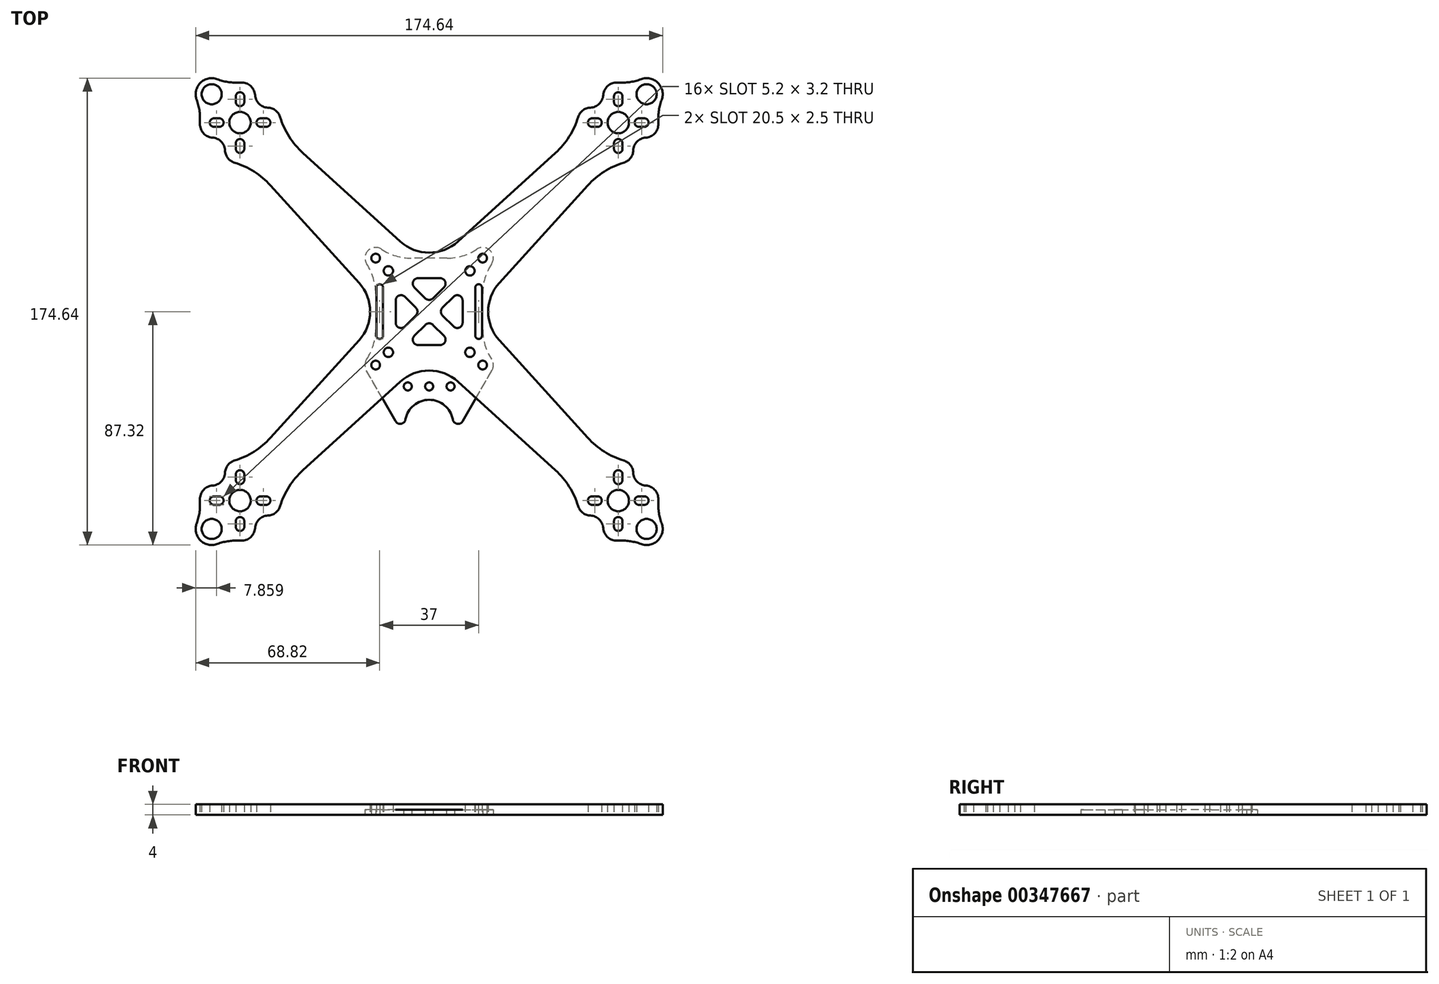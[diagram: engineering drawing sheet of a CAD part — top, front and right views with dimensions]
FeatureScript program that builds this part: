
annotation { "Feature Type Name" : "Feature", "Feature Type Description" : "" }
export const myFeature = defineFeature(function(context is Context, id is Id, definition is map)
    precondition{}
    {
        {
            var Q0;
            Q0=qCreatedBy(makeId("Top.planeOp"),FACE);
            var sketch = newSketch(context, id + "F0", { "sketchPlane" : qUnion([Q0])});
            skCircle(sketch, "E0", {"center": v(0, 0) * mm, "radius": 100 * mm, "construction": true});
            skArc(sketch, "E1", {"start": v(-59.34, 80.5) * mm, "mid": v(-59.71, 80.91) * mm, "end": v(-60.1, 81.32) * mm, "construction": true});
            skCircle(sketch, "E2", {"center": v(-70.71, 70.71) * mm, "radius": 4 * mm});
            skLineSegment(sketch, "E3", {"start": v(-70.71, 70.71) * mm, "end": v(0, 0) * mm, "construction": true});
            skCircle(sketch, "E4", {"center": v(-15.25, 15.25) * mm, "radius": 1.75 * mm});
            skCircle(sketch, "E5", {"center": v(-70.71, 70.71) * mm, "radius": 64.25 * mm, "construction": true});
            skCircle(sketch, "E6", {"center": v(-20, 20) * mm, "radius": 1.63 * mm});
            skCircle(sketch, "E7.MirrorC", {"center": v(20, 20) * mm, "radius": 1.63 * mm});
            skCircle(sketch, "E8.MirrorC", {"center": v(15.25, 15.25) * mm, "radius": 1.75 * mm});
            skCircle(sketch, "E9.MirrorC", {"center": v(-20, -20) * mm, "radius": 1.63 * mm});
            skCircle(sketch, "E10.MirrorC", {"center": v(20, -20) * mm, "radius": 1.63 * mm});
            skCircle(sketch, "E11.MirrorC", {"center": v(15.25, -15.25) * mm, "radius": 1.75 * mm});
            skCircle(sketch, "E12.MirrorC", {"center": v(-15.25, -15.25) * mm, "radius": 1.75 * mm});
            skArc(sketch, "E13.MirrorCS", {"start": v(59.34, 80.5) * mm, "mid": v(59.71, 80.91) * mm, "end": v(60.1, 81.32) * mm, "construction": true});
            skCircle(sketch, "E14.MirrorC", {"center": v(70.71, 70.71) * mm, "radius": 4 * mm});
            skArc(sketch, "E15.MirrorCS", {"start": v(-59.34, -80.5) * mm, "mid": v(-59.71, -80.91) * mm, "end": v(-60.1, -81.32) * mm, "construction": true});
            skCircle(sketch, "E16.MirrorC", {"center": v(-70.71, -70.71) * mm, "radius": 4 * mm});
            skArc(sketch, "E17.MirrorCS", {"start": v(59.34, -80.5) * mm, "mid": v(59.71, -80.91) * mm, "end": v(60.1, -81.32) * mm, "construction": true});
            skCircle(sketch, "E18.MirrorC", {"center": v(70.71, -70.71) * mm, "radius": 4 * mm});
            skLineSegment(sketch, "E19", {"start": v(-18.5, 9) * mm, "end": v(-18.5, -9) * mm, "construction": true});
            skArc(sketch, "E20.0.startCap", {"start": v(-19.75, 9) * mm, "mid": v(-18.5, 10.25) * mm, "end": v(-17.25, 9) * mm});
            skArc(sketch, "E20.0.endCap", {"start": v(-17.25, -9) * mm, "mid": v(-18.5, -10.25) * mm, "end": v(-19.75, -9) * mm});
            skLineSegment(sketch, "E20.0.left", {"start": v(-17.25, 9) * mm, "end": v(-17.25, -9) * mm});
            skLineSegment(sketch, "E20.0.right", {"start": v(-19.75, 9) * mm, "end": v(-19.75, -9) * mm});
            skLineSegment(sketch, "E21.MirrorCS", {"start": v(17.25, 9) * mm, "end": v(17.25, -9) * mm});
            skLineSegment(sketch, "E22.MirrorCS", {"start": v(18.5, 9) * mm, "end": v(18.5, -9) * mm, "construction": true});
            skArc(sketch, "E23.MirrorCS", {"start": v(17.25, -9) * mm, "mid": v(18.5, -10.25) * mm, "end": v(19.75, -9) * mm});
            skArc(sketch, "E24.MirrorCS", {"start": v(19.75, 9) * mm, "mid": v(18.5, 10.25) * mm, "end": v(17.25, 9) * mm});
            skLineSegment(sketch, "E25.MirrorCS", {"start": v(19.75, 9) * mm, "end": v(19.75, -9) * mm});
            skLineSegment(sketch, "E26", {"start": v(-12.5, 4.14) * mm, "end": v(-12.5, -4.14) * mm});
            skLineSegment(sketch, "E27", {"start": v(-9.09, -5.55) * mm, "end": v(-4.95, -1.41) * mm});
            skLineSegment(sketch, "E28", {"start": v(-4.95, 1.41) * mm, "end": v(-9.09, 5.55) * mm});
            skPoint(sketch, "E29.visualSharp", {"position": v(-12.5, 8.96) * mm});
            skArc(sketch, "E29.filletArc", {"start": v(-9.09, 5.55) * mm, "mid": v(-11.27, 5.98) * mm, "end": v(-12.5, 4.14) * mm});
            skPoint(sketch, "E30.visualSharp", {"position": v(-12.5, -8.96) * mm});
            skArc(sketch, "E30.filletArc", {"start": v(-12.5, -4.14) * mm, "mid": v(-11.27, -5.98) * mm, "end": v(-9.09, -5.55) * mm});
            skPoint(sketch, "E31.visualSharp", {"position": v(-3.54, 0) * mm});
            skArc(sketch, "E31.filletArc", {"start": v(-4.95, -1.41) * mm, "mid": v(-4.36, 0) * mm, "end": v(-4.95, 1.41) * mm});
            skArc(sketch, "E32.1.0", {"start": v(4.14, -12.5) * mm, "mid": v(5.98, -11.27) * mm, "end": v(5.55, -9.09) * mm});
            skPoint(sketch, "E32.1.1", {"position": v(0, -3.54) * mm});
            skLineSegment(sketch, "E32.1.2", {"start": v(-1.41, -4.95) * mm, "end": v(-5.55, -9.09) * mm});
            skArc(sketch, "E32.1.3", {"start": v(-5.55, -9.09) * mm, "mid": v(-5.98, -11.27) * mm, "end": v(-4.14, -12.5) * mm});
            skLineSegment(sketch, "E32.1.4", {"start": v(5.55, -9.09) * mm, "end": v(1.41, -4.95) * mm});
            skLineSegment(sketch, "E32.1.5", {"start": v(-4.14, -12.5) * mm, "end": v(4.14, -12.5) * mm});
            skArc(sketch, "E32.1.6", {"start": v(1.41, -4.95) * mm, "mid": v(0, -4.36) * mm, "end": v(-1.41, -4.95) * mm});
            skArc(sketch, "E32.2.0", {"start": v(12.5, 4.14) * mm, "mid": v(11.27, 5.98) * mm, "end": v(9.09, 5.55) * mm});
            skPoint(sketch, "E32.2.1", {"position": v(3.54, 0) * mm});
            skLineSegment(sketch, "E32.2.2", {"start": v(4.95, -1.41) * mm, "end": v(9.09, -5.55) * mm});
            skArc(sketch, "E32.2.3", {"start": v(9.09, -5.55) * mm, "mid": v(11.27, -5.98) * mm, "end": v(12.5, -4.14) * mm});
            skLineSegment(sketch, "E32.2.4", {"start": v(9.09, 5.55) * mm, "end": v(4.95, 1.41) * mm});
            skLineSegment(sketch, "E32.2.5", {"start": v(12.5, -4.14) * mm, "end": v(12.5, 4.14) * mm});
            skArc(sketch, "E32.2.6", {"start": v(4.95, 1.41) * mm, "mid": v(4.36, 0) * mm, "end": v(4.95, -1.41) * mm});
            skArc(sketch, "E32.3.0", {"start": v(-4.14, 12.5) * mm, "mid": v(-5.98, 11.27) * mm, "end": v(-5.55, 9.09) * mm});
            skPoint(sketch, "E32.3.1", {"position": v(0, 3.54) * mm});
            skLineSegment(sketch, "E32.3.2", {"start": v(1.41, 4.95) * mm, "end": v(5.55, 9.09) * mm});
            skArc(sketch, "E32.3.3", {"start": v(5.55, 9.09) * mm, "mid": v(5.98, 11.27) * mm, "end": v(4.14, 12.5) * mm});
            skLineSegment(sketch, "E32.3.4", {"start": v(-5.55, 9.09) * mm, "end": v(-1.41, 4.95) * mm});
            skLineSegment(sketch, "E32.3.5", {"start": v(4.14, 12.5) * mm, "end": v(-4.14, 12.5) * mm});
            skArc(sketch, "E32.3.6", {"start": v(-1.41, 4.95) * mm, "mid": v(0, 4.36) * mm, "end": v(1.41, 4.95) * mm});
            skCircle(sketch, "E33", {"center": v(-70.71, 70.71) * mm, "radius": 7.75 * mm, "construction": true});
            skCircle(sketch, "E34", {"center": v(-70.71, 70.71) * mm, "radius": 9.75 * mm, "construction": true});
            skLineSegment(sketch, "E35", {"start": v(-70.71, 70.71) * mm, "end": v(-70.71, 78.46) * mm, "construction": true});
            skLineSegment(sketch, "E36", {"start": v(-70.71, 78.46) * mm, "end": v(-70.71, 80.46) * mm, "construction": true});
            skArc(sketch, "E37.0.startCap", {"start": v(-69.11, 78.46) * mm, "mid": v(-70.71, 76.86) * mm, "end": v(-72.31, 78.46) * mm});
            skArc(sketch, "E37.0.endCap", {"start": v(-72.31, 80.46) * mm, "mid": v(-70.71, 82.06) * mm, "end": v(-69.11, 80.46) * mm});
            skLineSegment(sketch, "E37.0.left", {"start": v(-72.31, 78.46) * mm, "end": v(-72.31, 80.46) * mm});
            skLineSegment(sketch, "E37.0.right", {"start": v(-69.11, 78.46) * mm, "end": v(-69.11, 80.46) * mm});
            skLineSegment(sketch, "E38.1.0", {"start": v(-78.46, 72.31) * mm, "end": v(-80.46, 72.31) * mm});
            skLineSegment(sketch, "E38.1.1", {"start": v(-78.46, 69.11) * mm, "end": v(-80.46, 69.11) * mm});
            skArc(sketch, "E38.1.2", {"start": v(-80.46, 69.11) * mm, "mid": v(-82.06, 70.71) * mm, "end": v(-80.46, 72.31) * mm});
            skArc(sketch, "E38.1.3", {"start": v(-78.46, 72.31) * mm, "mid": v(-76.86, 70.71) * mm, "end": v(-78.46, 69.11) * mm});
            skLineSegment(sketch, "E38.1.4", {"start": v(-78.46, 70.71) * mm, "end": v(-80.46, 70.71) * mm, "construction": true});
            skLineSegment(sketch, "E38.2.0", {"start": v(-72.31, 62.96) * mm, "end": v(-72.31, 60.96) * mm});
            skLineSegment(sketch, "E38.2.1", {"start": v(-69.11, 62.96) * mm, "end": v(-69.11, 60.96) * mm});
            skArc(sketch, "E38.2.2", {"start": v(-69.11, 60.96) * mm, "mid": v(-70.71, 59.36) * mm, "end": v(-72.31, 60.96) * mm});
            skArc(sketch, "E38.2.3", {"start": v(-72.31, 62.96) * mm, "mid": v(-70.71, 64.56) * mm, "end": v(-69.11, 62.96) * mm});
            skLineSegment(sketch, "E38.2.4", {"start": v(-70.71, 62.96) * mm, "end": v(-70.71, 60.96) * mm, "construction": true});
            skLineSegment(sketch, "E38.3.0", {"start": v(-62.96, 69.11) * mm, "end": v(-60.96, 69.11) * mm});
            skLineSegment(sketch, "E38.3.1", {"start": v(-62.96, 72.31) * mm, "end": v(-60.96, 72.31) * mm});
            skArc(sketch, "E38.3.2", {"start": v(-60.96, 72.31) * mm, "mid": v(-59.36, 70.71) * mm, "end": v(-60.96, 69.11) * mm});
            skArc(sketch, "E38.3.3", {"start": v(-62.96, 69.11) * mm, "mid": v(-64.56, 70.71) * mm, "end": v(-62.96, 72.31) * mm});
            skLineSegment(sketch, "E38.3.4", {"start": v(-62.96, 70.71) * mm, "end": v(-60.96, 70.71) * mm, "construction": true});
            skArc(sketch, "E39", {"start": v(-79.22, 86.94) * mm, "mid": v(-85.56, 85.56) * mm, "end": v(-86.94, 79.22) * mm});
            skArc(sketch, "E40.trimOffspring", {"start": v(-85.7, 71.36) * mm, "mid": v(-85.4, 67.68) * mm, "end": v(-84.21, 64.18) * mm});
            skLineSegment(sketch, "E41", {"start": v(-70.71, 70.71) * mm, "end": v(-81.32, 81.32) * mm, "construction": true});
            skPoint(sketch, "E42.visualSharp", {"position": v(-84.63, 76.31) * mm});
            skArc(sketch, "E42.filletArc", {"start": v(-85.7, 71.36) * mm, "mid": v(-85.92, 75.35) * mm, "end": v(-86.94, 79.22) * mm});
            skPoint(sketch, "E43.visualSharp", {"position": v(-76.31, 84.63) * mm});
            skArc(sketch, "E43.filletArc", {"start": v(-79.22, 86.94) * mm, "mid": v(-75.35, 85.92) * mm, "end": v(-71.36, 85.7) * mm});
            skCircle(sketch, "E44", {"center": v(-81.32, 81.32) * mm, "radius": 3.75 * mm});
            skCircle(sketch, "E45.MirrorC", {"center": v(81.32, 81.32) * mm, "radius": 3.75 * mm});
            skArc(sketch, "E46.MirrorCS", {"start": v(79.22, 86.94) * mm, "mid": v(85.56, 85.56) * mm, "end": v(86.94, 79.22) * mm});
            skArc(sketch, "E47.MirrorCS", {"start": v(85.7, 71.36) * mm, "mid": v(85.92, 75.35) * mm, "end": v(86.94, 79.22) * mm});
            skArc(sketch, "E48.MirrorCS", {"start": v(79.22, 86.94) * mm, "mid": v(75.35, 85.92) * mm, "end": v(71.36, 85.7) * mm});
            skLineSegment(sketch, "E49.MirrorCS", {"start": v(72.31, 78.46) * mm, "end": v(72.31, 80.46) * mm});
            skArc(sketch, "E50.MirrorCS", {"start": v(72.31, 80.46) * mm, "mid": v(70.71, 82.06) * mm, "end": v(69.11, 80.46) * mm});
            skArc(sketch, "E51.MirrorCS", {"start": v(69.11, 78.46) * mm, "mid": v(70.71, 76.86) * mm, "end": v(72.31, 78.46) * mm});
            skLineSegment(sketch, "E52.MirrorCS", {"start": v(70.71, 78.46) * mm, "end": v(70.71, 80.46) * mm, "construction": true});
            skLineSegment(sketch, "E53.MirrorCS", {"start": v(69.11, 78.46) * mm, "end": v(69.11, 80.46) * mm});
            skArc(sketch, "E54.MirrorCS", {"start": v(60.96, 72.31) * mm, "mid": v(59.36, 70.71) * mm, "end": v(60.96, 69.11) * mm});
            skArc(sketch, "E55.MirrorCS", {"start": v(62.96, 69.11) * mm, "mid": v(64.56, 70.71) * mm, "end": v(62.96, 72.31) * mm});
            skLineSegment(sketch, "E56.MirrorCS", {"start": v(62.96, 70.71) * mm, "end": v(60.96, 70.71) * mm, "construction": true});
            skLineSegment(sketch, "E57.MirrorCS", {"start": v(62.96, 72.31) * mm, "end": v(60.96, 72.31) * mm});
            skLineSegment(sketch, "E58.MirrorCS", {"start": v(62.96, 69.11) * mm, "end": v(60.96, 69.11) * mm});
            skLineSegment(sketch, "E59.MirrorCS", {"start": v(69.11, 62.96) * mm, "end": v(69.11, 60.96) * mm});
            skArc(sketch, "E60.MirrorCS", {"start": v(72.31, 62.96) * mm, "mid": v(70.71, 64.56) * mm, "end": v(69.11, 62.96) * mm});
            skArc(sketch, "E61.MirrorCS", {"start": v(69.11, 60.96) * mm, "mid": v(70.71, 59.36) * mm, "end": v(72.31, 60.96) * mm});
            skLineSegment(sketch, "E62.MirrorCS", {"start": v(70.71, 62.96) * mm, "end": v(70.71, 60.96) * mm, "construction": true});
            skLineSegment(sketch, "E63.MirrorCS", {"start": v(72.31, 62.96) * mm, "end": v(72.31, 60.96) * mm});
            skArc(sketch, "E64.MirrorCS", {"start": v(78.46, 72.31) * mm, "mid": v(76.86, 70.71) * mm, "end": v(78.46, 69.11) * mm});
            skArc(sketch, "E65.MirrorCS", {"start": v(80.46, 69.11) * mm, "mid": v(82.06, 70.71) * mm, "end": v(80.46, 72.31) * mm});
            skLineSegment(sketch, "E66.MirrorCS", {"start": v(78.46, 69.11) * mm, "end": v(80.46, 69.11) * mm});
            skLineSegment(sketch, "E67.MirrorCS", {"start": v(78.46, 72.31) * mm, "end": v(80.46, 72.31) * mm});
            skLineSegment(sketch, "E68.MirrorCS", {"start": v(78.46, 70.71) * mm, "end": v(80.46, 70.71) * mm, "construction": true});
            skCircle(sketch, "E69.MirrorC", {"center": v(81.32, -81.32) * mm, "radius": 3.75 * mm});
            skCircle(sketch, "E70.MirrorC", {"center": v(-81.32, -81.32) * mm, "radius": 3.75 * mm});
            skArc(sketch, "E71.MirrorCS", {"start": v(-79.22, -86.94) * mm, "mid": v(-85.56, -85.56) * mm, "end": v(-86.94, -79.22) * mm});
            skArc(sketch, "E72.MirrorCS", {"start": v(-79.22, -86.94) * mm, "mid": v(-75.35, -85.92) * mm, "end": v(-71.36, -85.7) * mm});
            skArc(sketch, "E73.MirrorCS", {"start": v(-85.7, -71.36) * mm, "mid": v(-85.92, -75.35) * mm, "end": v(-86.94, -79.22) * mm});
            skArc(sketch, "E74.MirrorCS", {"start": v(79.22, -86.94) * mm, "mid": v(75.35, -85.92) * mm, "end": v(71.36, -85.7) * mm});
            skArc(sketch, "E75.MirrorCS", {"start": v(85.7, -71.36) * mm, "mid": v(85.92, -75.35) * mm, "end": v(86.94, -79.22) * mm});
            skArc(sketch, "E76.MirrorCS", {"start": v(79.22, -86.94) * mm, "mid": v(85.56, -85.56) * mm, "end": v(86.94, -79.22) * mm});
            skLineSegment(sketch, "E77.MirrorCS", {"start": v(69.11, -78.46) * mm, "end": v(69.11, -80.46) * mm});
            skLineSegment(sketch, "E78.MirrorCS", {"start": v(72.31, -78.46) * mm, "end": v(72.31, -80.46) * mm});
            skArc(sketch, "E79.MirrorCS", {"start": v(69.11, -78.46) * mm, "mid": v(70.71, -76.86) * mm, "end": v(72.31, -78.46) * mm});
            skLineSegment(sketch, "E80.MirrorCS", {"start": v(70.71, -78.46) * mm, "end": v(70.71, -80.46) * mm, "construction": true});
            skArc(sketch, "E81.MirrorCS", {"start": v(72.31, -80.46) * mm, "mid": v(70.71, -82.06) * mm, "end": v(69.11, -80.46) * mm});
            skLineSegment(sketch, "E82.MirrorCS", {"start": v(78.46, -70.71) * mm, "end": v(80.46, -70.71) * mm, "construction": true});
            skArc(sketch, "E83.MirrorCS", {"start": v(78.46, -72.31) * mm, "mid": v(76.86, -70.71) * mm, "end": v(78.46, -69.11) * mm});
            skArc(sketch, "E84.MirrorCS", {"start": v(80.46, -69.11) * mm, "mid": v(82.06, -70.71) * mm, "end": v(80.46, -72.31) * mm});
            skLineSegment(sketch, "E85.MirrorCS", {"start": v(78.46, -69.11) * mm, "end": v(80.46, -69.11) * mm});
            skLineSegment(sketch, "E86.MirrorCS", {"start": v(78.46, -72.31) * mm, "end": v(80.46, -72.31) * mm});
            skArc(sketch, "E87.MirrorCS", {"start": v(72.31, -62.96) * mm, "mid": v(70.71, -64.56) * mm, "end": v(69.11, -62.96) * mm});
            skLineSegment(sketch, "E88.MirrorCS", {"start": v(69.11, -62.96) * mm, "end": v(69.11, -60.96) * mm});
            skArc(sketch, "E89.MirrorCS", {"start": v(69.11, -60.96) * mm, "mid": v(70.71, -59.36) * mm, "end": v(72.31, -60.96) * mm});
            skLineSegment(sketch, "E90.MirrorCS", {"start": v(70.71, -62.96) * mm, "end": v(70.71, -60.96) * mm, "construction": true});
            skLineSegment(sketch, "E91.MirrorCS", {"start": v(72.31, -62.96) * mm, "end": v(72.31, -60.96) * mm});
            skLineSegment(sketch, "E92.MirrorCS", {"start": v(62.96, -72.31) * mm, "end": v(60.96, -72.31) * mm});
            skLineSegment(sketch, "E93.MirrorCS", {"start": v(62.96, -70.71) * mm, "end": v(60.96, -70.71) * mm, "construction": true});
            skArc(sketch, "E94.MirrorCS", {"start": v(62.96, -69.11) * mm, "mid": v(64.56, -70.71) * mm, "end": v(62.96, -72.31) * mm});
            skArc(sketch, "E95.MirrorCS", {"start": v(60.96, -72.31) * mm, "mid": v(59.36, -70.71) * mm, "end": v(60.96, -69.11) * mm});
            skLineSegment(sketch, "E96.MirrorCS", {"start": v(62.96, -69.11) * mm, "end": v(60.96, -69.11) * mm});
            skLineSegment(sketch, "E97.MirrorCS", {"start": v(-72.31, -78.46) * mm, "end": v(-72.31, -80.46) * mm});
            skLineSegment(sketch, "E98.MirrorCS", {"start": v(-69.11, -78.46) * mm, "end": v(-69.11, -80.46) * mm});
            skArc(sketch, "E99.MirrorCS", {"start": v(-69.11, -78.46) * mm, "mid": v(-70.71, -76.86) * mm, "end": v(-72.31, -78.46) * mm});
            skArc(sketch, "E100.MirrorCS", {"start": v(-72.31, -80.46) * mm, "mid": v(-70.71, -82.06) * mm, "end": v(-69.11, -80.46) * mm});
            skLineSegment(sketch, "E101.MirrorCS", {"start": v(-70.71, -78.46) * mm, "end": v(-70.71, -80.46) * mm, "construction": true});
            skLineSegment(sketch, "E102.MirrorCS", {"start": v(-62.96, -70.71) * mm, "end": v(-60.96, -70.71) * mm, "construction": true});
            skArc(sketch, "E103.MirrorCS", {"start": v(-62.96, -69.11) * mm, "mid": v(-64.56, -70.71) * mm, "end": v(-62.96, -72.31) * mm});
            skLineSegment(sketch, "E104.MirrorCS", {"start": v(-62.96, -69.11) * mm, "end": v(-60.96, -69.11) * mm});
            skLineSegment(sketch, "E105.MirrorCS", {"start": v(-62.96, -72.31) * mm, "end": v(-60.96, -72.31) * mm});
            skArc(sketch, "E106.MirrorCS", {"start": v(-60.96, -72.31) * mm, "mid": v(-59.36, -70.71) * mm, "end": v(-60.96, -69.11) * mm});
            skLineSegment(sketch, "E107.MirrorCS", {"start": v(-70.71, -62.96) * mm, "end": v(-70.71, -60.96) * mm, "construction": true});
            skLineSegment(sketch, "E108.MirrorCS", {"start": v(-72.31, -62.96) * mm, "end": v(-72.31, -60.96) * mm});
            skLineSegment(sketch, "E109.MirrorCS", {"start": v(-69.11, -62.96) * mm, "end": v(-69.11, -60.96) * mm});
            skArc(sketch, "E110.MirrorCS", {"start": v(-72.31, -62.96) * mm, "mid": v(-70.71, -64.56) * mm, "end": v(-69.11, -62.96) * mm});
            skArc(sketch, "E111.MirrorCS", {"start": v(-69.11, -60.96) * mm, "mid": v(-70.71, -59.36) * mm, "end": v(-72.31, -60.96) * mm});
            skLineSegment(sketch, "E112.MirrorCS", {"start": v(-78.46, -69.11) * mm, "end": v(-80.46, -69.11) * mm});
            skLineSegment(sketch, "E113.MirrorCS", {"start": v(-78.46, -72.31) * mm, "end": v(-80.46, -72.31) * mm});
            skArc(sketch, "E114.MirrorCS", {"start": v(-78.46, -72.31) * mm, "mid": v(-76.86, -70.71) * mm, "end": v(-78.46, -69.11) * mm});
            skArc(sketch, "E115.MirrorCS", {"start": v(-80.46, -69.11) * mm, "mid": v(-82.06, -70.71) * mm, "end": v(-80.46, -72.31) * mm});
            skLineSegment(sketch, "E116.MirrorCS", {"start": v(-78.46, -70.71) * mm, "end": v(-80.46, -70.71) * mm, "construction": true});
            skArc(sketch, "E117.trimOffspring", {"start": v(-85.7, -71.36) * mm, "mid": v(-85.4, -67.68) * mm, "end": v(-84.21, -64.18) * mm});
            skLineSegment(sketch, "E118", {"start": v(-70.71, 70.71) * mm, "end": v(-60.1, 81.32) * mm, "construction": true});
            skArc(sketch, "E119", {"start": v(-64.18, 84.21) * mm, "mid": v(-63.64, 77.78) * mm, "end": v(-57.2, 77.24) * mm});
            skArc(sketch, "E120.trimOffspring", {"start": v(-64.18, 84.21) * mm, "mid": v(-67.68, 85.4) * mm, "end": v(-71.36, 85.7) * mm});
            skArc(sketch, "E121.MirrorCS", {"start": v(-84.21, 64.18) * mm, "mid": v(-77.78, 63.64) * mm, "end": v(-77.24, 57.2) * mm});
            skArc(sketch, "E122.trimOffspring", {"start": v(-81.32, 60.1) * mm, "mid": v(-80.91, 59.71) * mm, "end": v(-80.5, 59.34) * mm, "construction": true});
            skArc(sketch, "E123.MirrorCS", {"start": v(64.18, 84.21) * mm, "mid": v(63.64, 77.78) * mm, "end": v(57.2, 77.24) * mm});
            skArc(sketch, "E124.MirrorCS", {"start": v(84.21, 64.18) * mm, "mid": v(77.78, 63.64) * mm, "end": v(77.24, 57.2) * mm});
            skArc(sketch, "E125.MirrorCS", {"start": v(84.21, -64.18) * mm, "mid": v(77.78, -63.64) * mm, "end": v(77.24, -57.2) * mm});
            skArc(sketch, "E126.MirrorCS", {"start": v(64.18, -84.21) * mm, "mid": v(63.64, -77.78) * mm, "end": v(57.2, -77.24) * mm});
            skArc(sketch, "E127.MirrorCS", {"start": v(-84.21, -64.18) * mm, "mid": v(-77.78, -63.64) * mm, "end": v(-77.24, -57.2) * mm});
            skArc(sketch, "E128.MirrorCS", {"start": v(-64.18, -84.21) * mm, "mid": v(-63.64, -77.78) * mm, "end": v(-57.2, -77.24) * mm});
            skArc(sketch, "E129.trimOffspring", {"start": v(-81.32, -60.1) * mm, "mid": v(-80.91, -59.71) * mm, "end": v(-80.5, -59.34) * mm, "construction": true});
            skArc(sketch, "E130.trimOffspring", {"start": v(64.18, -84.21) * mm, "mid": v(67.68, -85.4) * mm, "end": v(71.36, -85.7) * mm});
            skLineSegment(sketch, "E131", {"start": v(70.71, 70.71) * mm, "end": v(81.32, 81.32) * mm, "construction": true});
            skArc(sketch, "E132.MirrorCS", {"start": v(80.5, 59.34) * mm, "mid": v(80.91, 59.71) * mm, "end": v(81.32, 60.1) * mm, "construction": true});
            skArc(sketch, "E133.trimOffspring", {"start": v(84.21, 64.18) * mm, "mid": v(85.4, 67.68) * mm, "end": v(85.7, 71.36) * mm});
            skArc(sketch, "E134.MirrorCS", {"start": v(84.21, -64.18) * mm, "mid": v(85.4, -67.68) * mm, "end": v(85.7, -71.36) * mm});
            skArc(sketch, "E135.trimOffspring", {"start": v(64.18, 84.21) * mm, "mid": v(67.68, 85.4) * mm, "end": v(71.36, 85.7) * mm});
            skArc(sketch, "E136.trimOffspring", {"start": v(-64.18, -84.21) * mm, "mid": v(-67.68, -85.4) * mm, "end": v(-71.36, -85.7) * mm});
            skArc(sketch, "E137", {"start": v(-77.24, 57.2) * mm, "mid": v(-75.8, 56.6) * mm, "end": v(-74.32, 56.15) * mm});
            skLineSegment(sketch, "E138", {"start": v(-47.2, 59.33) * mm, "end": v(-10.76, 26.23) * mm});
            skLineSegment(sketch, "E139", {"start": v(-59.33, 47.2) * mm, "end": v(-26.23, 10.76) * mm});
            skArc(sketch, "E140.trimOffspring", {"start": v(-56.15, 74.32) * mm, "mid": v(-56.6, 75.8) * mm, "end": v(-57.2, 77.24) * mm});
            skPoint(sketch, "E141.visualSharp", {"position": v(-67.4, 56.08) * mm});
            skArc(sketch, "E141.filletArc", {"start": v(-59.33, 47.2) * mm, "mid": v(-66.16, 52.8) * mm, "end": v(-74.32, 56.15) * mm});
            skPoint(sketch, "E142.visualSharp", {"position": v(-56.08, 67.4) * mm});
            skArc(sketch, "E142.filletArc", {"start": v(-56.15, 74.32) * mm, "mid": v(-52.8, 66.16) * mm, "end": v(-47.2, 59.33) * mm});
            skLineSegment(sketch, "E143.MirrorCS", {"start": v(47.2, 59.33) * mm, "end": v(10.76, 26.23) * mm});
            skArc(sketch, "E144.MirrorCS", {"start": v(56.15, 74.32) * mm, "mid": v(52.8, 66.16) * mm, "end": v(47.2, 59.33) * mm});
            skArc(sketch, "E145.MirrorCS", {"start": v(56.15, 74.32) * mm, "mid": v(56.6, 75.8) * mm, "end": v(57.2, 77.24) * mm});
            skLineSegment(sketch, "E146.MirrorCS", {"start": v(59.33, 47.2) * mm, "end": v(26.23, 10.76) * mm});
            skArc(sketch, "E147.MirrorCS", {"start": v(59.33, 47.2) * mm, "mid": v(66.16, 52.8) * mm, "end": v(74.32, 56.15) * mm});
            skArc(sketch, "E148.MirrorCS", {"start": v(77.24, 57.2) * mm, "mid": v(75.8, 56.6) * mm, "end": v(74.32, 56.15) * mm});
            skPoint(sketch, "E149.visualSharp", {"position": v(0, 16.45) * mm});
            skArc(sketch, "E149.filletArc", {"start": v(-10.76, 26.23) * mm, "mid": v(0, 22.07) * mm, "end": v(10.76, 26.23) * mm});
            skLineSegment(sketch, "E150.MirrorCS", {"start": v(-59.33, -47.2) * mm, "end": v(-26.23, -10.76) * mm});
            skLineSegment(sketch, "E151.MirrorCS", {"start": v(-47.2, -59.33) * mm, "end": v(-10.76, -26.23) * mm});
            skLineSegment(sketch, "E152.MirrorCS", {"start": v(47.2, -59.33) * mm, "end": v(10.76, -26.23) * mm});
            skLineSegment(sketch, "E153.MirrorCS", {"start": v(59.33, -47.2) * mm, "end": v(26.23, -10.76) * mm});
            skArc(sketch, "E154.MirrorCS", {"start": v(-10.76, -26.23) * mm, "mid": v(0, -22.07) * mm, "end": v(10.76, -26.23) * mm});
            skArc(sketch, "E155.MirrorCS", {"start": v(-59.33, -47.2) * mm, "mid": v(-66.16, -52.8) * mm, "end": v(-74.32, -56.15) * mm});
            skArc(sketch, "E156.MirrorCS", {"start": v(-56.15, -74.32) * mm, "mid": v(-52.8, -66.16) * mm, "end": v(-47.2, -59.33) * mm});
            skArc(sketch, "E157.MirrorCS", {"start": v(-77.24, -57.2) * mm, "mid": v(-75.8, -56.6) * mm, "end": v(-74.32, -56.15) * mm});
            skArc(sketch, "E158.MirrorCS", {"start": v(-56.15, -74.32) * mm, "mid": v(-56.6, -75.8) * mm, "end": v(-57.2, -77.24) * mm});
            skArc(sketch, "E159.MirrorCS", {"start": v(77.24, -57.2) * mm, "mid": v(75.8, -56.6) * mm, "end": v(74.32, -56.15) * mm});
            skArc(sketch, "E160.MirrorCS", {"start": v(59.33, -47.2) * mm, "mid": v(66.16, -52.8) * mm, "end": v(74.32, -56.15) * mm});
            skArc(sketch, "E161.MirrorCS", {"start": v(56.15, -74.32) * mm, "mid": v(56.6, -75.8) * mm, "end": v(57.2, -77.24) * mm});
            skArc(sketch, "E162.MirrorCS", {"start": v(56.15, -74.32) * mm, "mid": v(52.8, -66.16) * mm, "end": v(47.2, -59.33) * mm});
            skArc(sketch, "E163", {"start": v(-26.23, -10.76) * mm, "mid": v(-22.07, 0) * mm, "end": v(-26.23, 10.76) * mm});
            skPoint(sketch, "E164.orphan", {"position": v(-16.45, 0) * mm});
            skArc(sketch, "E165.MirrorCS", {"start": v(26.23, -10.76) * mm, "mid": v(22.07, 0) * mm, "end": v(26.23, 10.76) * mm});
            skPoint(sketch, "E166.trimOffspring.end.orphan", {"position": v(16.45, 0) * mm});
            skSolve(sketch);
        }
        {
            var Q0;
            Q0 = qSketchRegion(id + "F0", true);
            extrude(context, id + "F1", {"entities" : qUnion([Q0]), "depth" : 4 * mm, "offsetDistance" : 25 * mm});
        }
        {
            var Q0;
            Q0=makeQuery(id+"F1.opExtrude","SWEPT_EDGE",EDGE,{"disambiguationData":[OSD([sQuery(id+"F0.wireOp",EDGE,"E40.trimOffspring"),sQuery(id+"F0.wireOp",EDGE,"E121.MirrorCS")])]});
            var Q1;
            Q1=makeQuery(id+"F1.opExtrude","SWEPT_EDGE",EDGE,{"disambiguationData":[OSD([sQuery(id+"F0.wireOp",EDGE,"2OzgBHEG-699r-rUpt-6WqC-xNI9DFPUQxpt"),sQuery(id+"F0.wireOp",EDGE,"E121.MirrorCS")])]});
            var Q2;
            Q2=makeQuery(id+"F1.opExtrude","SWEPT_EDGE",EDGE,{"disambiguationData":[OSD([sQuery(id+"F0.wireOp",EDGE,"E119"),sQuery(id+"F0.wireOp",EDGE,"E120.trimOffspring")])]});
            var Q3;
            Q3=makeQuery(id+"F1.opExtrude","SWEPT_EDGE",EDGE,{"disambiguationData":[OSD([sQuery(id+"F0.wireOp",EDGE,"thRzdSz5-VkX9-QmSb-G7Lu-axPsin1qlEUI"),sQuery(id+"F0.wireOp",EDGE,"E119")])]});
            var Q4;
            Q4=makeQuery(id+"F1.opExtrude","SWEPT_EDGE",EDGE,{"disambiguationData":[OSD([sQuery(id+"F0.wireOp",EDGE,"0db81048-8270-4a98-9683-425ff5c905a50.MirrorCS"),sQuery(id+"F0.wireOp",EDGE,"E123.MirrorCS")])]});
            var Q5;
            Q5=makeQuery(id+"F1.opExtrude","SWEPT_EDGE",EDGE,{"disambiguationData":[OSD([sQuery(id+"F0.wireOp",EDGE,"E123.MirrorCS"),sQuery(id+"F0.wireOp",EDGE,"E135.trimOffspring")])]});
            var Q6;
            Q6=makeQuery(id+"F1.opExtrude","SWEPT_EDGE",EDGE,{"disambiguationData":[OSD([sQuery(id+"F0.wireOp",EDGE,"105c790f-be80-4801-8d80-55a60396899c0.MirrorCS"),sQuery(id+"F0.wireOp",EDGE,"E124.MirrorCS")])]});
            var Q7;
            Q7=makeQuery(id+"F1.opExtrude","SWEPT_EDGE",EDGE,{"disambiguationData":[OSD([sQuery(id+"F0.wireOp",EDGE,"E124.MirrorCS"),sQuery(id+"F0.wireOp",EDGE,"E133.trimOffspring")])]});
            var Q8;
            Q8=makeQuery(id+"F1.opExtrude","SWEPT_EDGE",EDGE,{"disambiguationData":[OSD([sQuery(id+"F0.wireOp",EDGE,"b50099fd-6daf-4c94-a315-a15a4c68d0dd0.MirrorCS"),sQuery(id+"F0.wireOp",EDGE,"E126.MirrorCS")])]});
            var Q9;
            Q9=makeQuery(id+"F1.opExtrude","SWEPT_EDGE",EDGE,{"disambiguationData":[OSD([sQuery(id+"F0.wireOp",EDGE,"E126.MirrorCS"),sQuery(id+"F0.wireOp",EDGE,"E130.trimOffspring")])]});
            var Q10;
            Q10=makeQuery(id+"F1.opExtrude","SWEPT_EDGE",EDGE,{"disambiguationData":[OSD([sQuery(id+"F0.wireOp",EDGE,"E125.MirrorCS"),sQuery(id+"F0.wireOp",EDGE,"E134.MirrorCS")])]});
            var Q11;
            Q11=makeQuery(id+"F1.opExtrude","SWEPT_EDGE",EDGE,{"disambiguationData":[OSD([sQuery(id+"F0.wireOp",EDGE,"1bc4892f-81a8-4a28-a671-4a486100d4d30.MirrorCS"),sQuery(id+"F0.wireOp",EDGE,"E125.MirrorCS")])]});
            var Q12;
            Q12=makeQuery(id+"F1.opExtrude","SWEPT_EDGE",EDGE,{"disambiguationData":[OSD([sQuery(id+"F0.wireOp",EDGE,"E128.MirrorCS"),sQuery(id+"F0.wireOp",EDGE,"E136.trimOffspring")])]});
            var Q13;
            Q13=makeQuery(id+"F1.opExtrude","SWEPT_EDGE",EDGE,{"disambiguationData":[OSD([sQuery(id+"F0.wireOp",EDGE,"b3ab0ffb-c5e8-4cb3-bf82-160587da1c470.MirrorCS"),sQuery(id+"F0.wireOp",EDGE,"E128.MirrorCS")])]});
            var Q14;
            Q14=makeQuery(id+"F1.opExtrude","SWEPT_EDGE",EDGE,{"disambiguationData":[OSD([sQuery(id+"F0.wireOp",EDGE,"E117.trimOffspring"),sQuery(id+"F0.wireOp",EDGE,"E127.MirrorCS")])]});
            var Q15;
            Q15=makeQuery(id+"F1.opExtrude","SWEPT_EDGE",EDGE,{"disambiguationData":[OSD([sQuery(id+"F0.wireOp",EDGE,"d50168aa-1fc3-4232-a505-5d7b2a552cd40.MirrorCS"),sQuery(id+"F0.wireOp",EDGE,"E127.MirrorCS")])]});
            fillet(context, id + "F2", {"entities" : qUnion([Q0, Q1, Q2, Q3, Q4, Q5, Q6, Q7, Q8, Q9, Q10, Q11, Q12, Q13, Q14, Q15]), "radius" : 5 * mm, "tangentPropagation" : true, "allowEdgeOverflow" : false});
        }
        {
            var Q0;
            Q0=qCreatedBy(makeId("Top.planeOp"),FACE);
            var sketch = newSketch(context, id + "F3", { "sketchPlane" : qUnion([Q0])});
            skArc(sketch, "E167", {"start": v(-17.79, 23.33) * mm, "mid": v(-22.83, 22.83) * mm, "end": v(-23.33, 17.79) * mm});
            skCircle(sketch, "E168", {"center": v(-20, 20) * mm, "radius": 1.63 * mm});
            skLineSegment(sketch, "E169", {"start": v(-20, 6.73) * mm, "end": v(-20, 0) * mm});
            skLineSegment(sketch, "E170", {"start": v(-6.73, 20) * mm, "end": v(0, 20) * mm});
            skPoint(sketch, "E171.visualSharp", {"position": v(-20, 16) * mm});
            skArc(sketch, "E171.filletArc", {"start": v(-20, 6.73) * mm, "mid": v(-20.85, 12.5) * mm, "end": v(-23.33, 17.79) * mm});
            skPoint(sketch, "E172.visualSharp", {"position": v(-16, 20) * mm});
            skArc(sketch, "E172.filletArc", {"start": v(-17.79, 23.33) * mm, "mid": v(-12.5, 20.85) * mm, "end": v(-6.73, 20) * mm});
            skPoint(sketch, "E173.MirrorP", {"position": v(20, 16) * mm});
            skPoint(sketch, "E174.MirrorP", {"position": v(16, 20) * mm});
            skArc(sketch, "E175.MirrorCS", {"start": v(17.79, 23.33) * mm, "mid": v(22.83, 22.83) * mm, "end": v(23.33, 17.79) * mm});
            skCircle(sketch, "E176.MirrorC", {"center": v(20, 20) * mm, "radius": 1.63 * mm});
            skArc(sketch, "E177.MirrorCS", {"start": v(20, 6.73) * mm, "mid": v(20.85, 12.5) * mm, "end": v(23.33, 17.79) * mm});
            skArc(sketch, "E178.MirrorCS", {"start": v(17.79, 23.33) * mm, "mid": v(12.5, 20.85) * mm, "end": v(6.73, 20) * mm});
            skLineSegment(sketch, "E179.MirrorCS", {"start": v(20, 6.73) * mm, "end": v(20, 0) * mm});
            skLineSegment(sketch, "E180.MirrorCS", {"start": v(6.73, 20) * mm, "end": v(0, 20) * mm});
            skPoint(sketch, "E181.MirrorP", {"position": v(-16, -20) * mm});
            skArc(sketch, "E182.MirrorCS", {"start": v(-23.47, -22) * mm, "mid": v(-24, -19.87) * mm, "end": v(-23.33, -17.79) * mm});
            skCircle(sketch, "E183.MirrorC", {"center": v(-20, -20) * mm, "radius": 1.63 * mm});
            skPoint(sketch, "E184.MirrorP", {"position": v(20, -16) * mm});
            skPoint(sketch, "E185.MirrorP", {"position": v(16, -20) * mm});
            skArc(sketch, "E186.MirrorCS", {"start": v(20, -6.73) * mm, "mid": v(20.85, -12.5) * mm, "end": v(23.33, -17.79) * mm});
            skPoint(sketch, "E187.MirrorP", {"position": v(-20, -16) * mm});
            skCircle(sketch, "E188.MirrorC", {"center": v(20, -20) * mm, "radius": 1.63 * mm});
            skArc(sketch, "E189.MirrorCS", {"start": v(-20, -6.73) * mm, "mid": v(-20.85, -12.5) * mm, "end": v(-23.33, -17.79) * mm});
            skArc(sketch, "E190.MirrorCS", {"start": v(23.47, -22) * mm, "mid": v(24, -19.87) * mm, "end": v(23.33, -17.79) * mm});
            skLineSegment(sketch, "E191.MirrorCS", {"start": v(-20, -6.73) * mm, "end": v(-20, 0) * mm});
            skLineSegment(sketch, "E192.MirrorCS", {"start": v(20, -6.73) * mm, "end": v(20, 0) * mm});
            skCircle(sketch, "E193", {"center": v(0, -28) * mm, "radius": 1.5 * mm});
            skLineSegment(sketch, "E194", {"start": v(-12.55, -41) * mm, "end": v(-23.47, -22) * mm});
            skLineSegment(sketch, "E195.MirrorCS", {"start": v(12.55, -41) * mm, "end": v(23.47, -22) * mm});
            skPoint(sketch, "E196.orphan", {"position": v(17.79, -23.33) * mm});
            skCircle(sketch, "E197", {"center": v(-8, -28) * mm, "radius": 1.5 * mm});
            skCircle(sketch, "E198", {"center": v(8, -28) * mm, "radius": 1.5 * mm});
            skArc(sketch, "E199", {"start": v(8.85, -40.36) * mm, "mid": v(0, -33) * mm, "end": v(-8.85, -40.36) * mm});
            skArc(sketch, "E200.filletArc", {"start": v(-12.55, -41) * mm, "mid": v(-10.48, -41.97) * mm, "end": v(-8.85, -40.36) * mm});
            skArc(sketch, "E201.filletArc", {"start": v(8.85, -40.36) * mm, "mid": v(10.48, -41.97) * mm, "end": v(12.55, -41) * mm});
            skSolve(sketch);
        }
        {
            var Q0;
            Q0=makeQuery(id+"F3.imprint","IMPRINT",FACE,{"disambiguationData":[TD([[makeQuery(id+"F3.imprint","IMPRINT",EDGE,{"derivedFrom":sQuery(id+"F3.wireOp",EDGE,"E167")}),1.0]])]});
            extrude(context, id + "F4", {"entities" : qUnion([Q0]), "depth" : 2 * mm, "offsetDistance" : 25 * mm});
        }
    });
